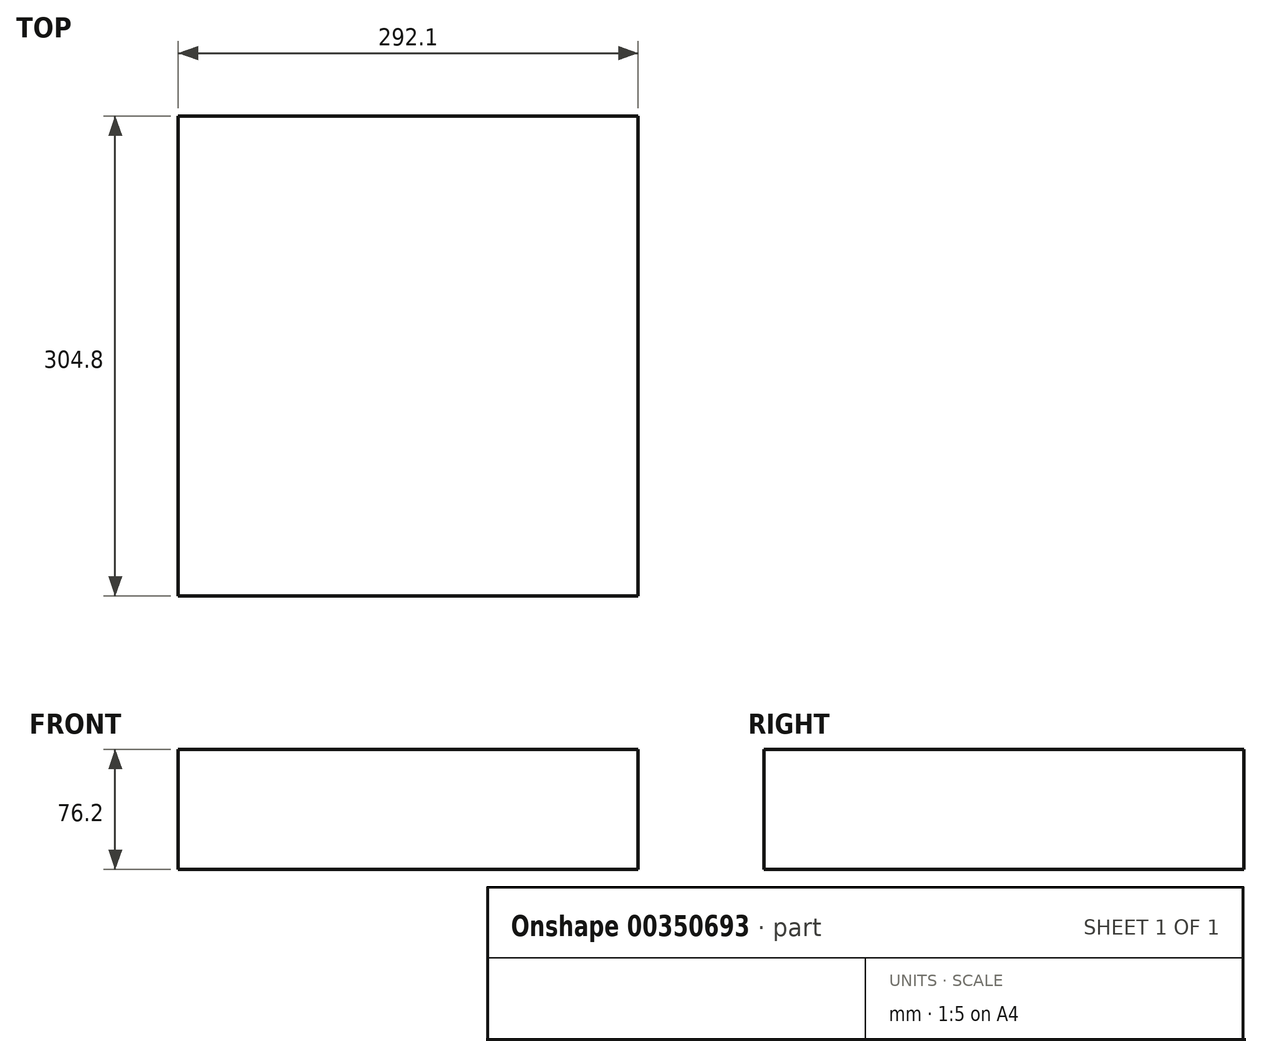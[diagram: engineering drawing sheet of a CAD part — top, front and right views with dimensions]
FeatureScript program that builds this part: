
annotation { "Feature Type Name" : "Feature", "Feature Type Description" : "" }
export const myFeature = defineFeature(function(context is Context, id is Id, definition is map)
    precondition{}
    {
        {
            var Q0;
            Q0=qCreatedBy(makeId("Front.planeOp"),FACE);
            var sketch = newSketch(context, id + "F0", { "sketchPlane" : qUnion([Q0])});
            skLineSegment(sketch, "E0.bottom", {"start": v(146.05, 42.65) * mm, "end": v(-146.05, 42.65) * mm});
            skLineSegment(sketch, "E0.top", {"start": v(146.05, -33.55) * mm, "end": v(-146.05, -33.55) * mm});
            skLineSegment(sketch, "E0.left", {"start": v(146.05, 42.65) * mm, "end": v(146.05, -33.55) * mm});
            skLineSegment(sketch, "E0.right", {"start": v(-146.05, 42.65) * mm, "end": v(-146.05, -33.55) * mm});
            skPoint(sketch, "E0.middle", {"position": v(0, 4.55) * mm});
            skSolve(sketch);
        }
        {
            var Q0;
            Q0=makeQuery(id+"F0.imprint","IMPRINT",FACE,{"disambiguationData":[TD([[makeQuery(id+"F0.imprint","IMPRINT",EDGE,{"derivedFrom":sQuery(id+"F0.wireOp",EDGE,"E0.bottom")}),1.0]])]});
            extrude(context, id + "F1", {"entities" : qUnion([Q0]), "oppositeDirection" : true, "depth" : 304.8 * mm});
        }
    });
